# Revit family: Levelers_Kelley_HK
name_source: partatom
category: Specialty Equipment
units: mm (PartAtom-declared; Revit-internal decimal feet)

## family parameters
Always vertical = Yes
Cut with Voids When Loaded = Yes
Enable Cutting in Views = No
Host = Floor
Maintain Annotation Orientation = No
Part Type = Normal
Room Calculation Point = No
Round Connector Dimension = Use Diameter
Shared = No

## types (24) — shared parameters
Capacity = 30-50K
Curb = 0' - 3"
Default Elevation = 0' - 0"
Description = Hydraulic Leveler
LipLength = 1' - 6"
Manufacturer = Kelley Entrematic
Model = HK
URL = http://kelleyentrematic.com

## per-type parameters (varying)
| type | LipExtension | PitDepth | PitDepthR | PitLength | PitWidth |
| 6x6 | 0' - 0" | 1' - 8" | 1' - 7 1/2" | 5' - 3" | 6' - 2" |
| 6x8 | 0' - 0" | 1' - 8" | 1' - 7 1/2" | 7' - 3" | 6' - 2" |
| 6.5x6 | 0' - 0" | 1' - 8" | 1' - 7 1/2" | 5' - 3" | 6' - 8" |
| 6.5x8 | 0' - 0" | 1' - 8" | 1' - 7 1/2" | 7' - 3" | 6' - 8" |
| 7x6 | 0' - 0" | 1' - 8" | 1' - 7 1/2" | 5' - 3" | 7' - 1" |
| 7x8 | 0' - 0" | 1' - 8" | 1' - 7 1/2" | 7' - 3" | 7' - 1" |
| 6x10 | 0' - 0" | 2' - 0" | 1' - 11 1/2" | 9' - 3" | 6' - 2" |
| 6.5x10 | 0' - 0" | 2' - 0" | 1' - 11 1/2" | 9' - 3" | 6' - 8" |
| 7x10 | 0' - 0" | 2' - 0" | 1' - 11 1/2" | 9' - 3" | 7' - 1" |
| 6x6 Barrier Lip | 0' - 5" | 1' - 8" | 1' - 7 1/2" | 5' - 3" | 6' - 2" |
| 6x8 Barrier Lip | 0' - 5" | 1' - 8" | 1' - 7 1/2" | 7' - 3" | 6' - 2" |
| 6x10 Barrier Lip | 0' - 5" | 2' - 0" | 1' - 11 1/2" | 9' - 3" | 6' - 2" |
| 7x10 Barrier Lip | 0' - 5" | 2' - 0" | 1' - 11 1/2" | 9' - 3" | 7' - 1" |
| 7x6 Barrier Lip | 0' - 5" | 1' - 8" | 1' - 7 1/2" | 5' - 3" | 7' - 1" |
| 7x8 Barrier Lip | 0' - 5" | 1' - 8" | 1' - 7 1/2" | 7' - 3" | 7' - 1" |
| 6.5x10 Barrier Lip | 0' - 5" | 2' - 0" | 1' - 11 1/2" | 9' - 3" | 6' - 8" |
| 6.5x6 Barrier Lip | 0' - 5" | 1' - 8" | 1' - 7 1/2" | 5' - 3" | 6' - 8" |
| 6.5x8 Barrier Lip | 0' - 5" | 1' - 8" | 1' - 7 1/2" | 7' - 3" | 6' - 8" |
| 6.5x12 | 0' - 0" | 2' - 0" | 1' - 11 1/2" | 11' - 3" | 6' - 8" |
| 6.5x12 Barrier Lip | 0' - 5" | 2' - 0" | 1' - 11 1/2" | 11' - 3" | 6' - 8" |
| 6x12 | 0' - 0" | 2' - 0" | 1' - 11 1/2" | 11' - 3" | 6' - 2" |
| 6x12 Barrier Lip | 0' - 5" | 2' - 0" | 1' - 11 1/2" | 11' - 3" | 6' - 2" |
| 7x12 | 0' - 0" | 2' - 0" | 1' - 11 1/2" | 11' - 3" | 7' - 1" |
| 7x12 Barrier Lip | 0' - 5" | 2' - 0" | 1' - 11 1/2" | 11' - 3" | 7' - 1" |

## geometry (parser evidence)
native form markers: Blend x4, Sweep x2
no freeform markers — native parametric forms only
